# Revit family: Hager-IC-IP40-Plain_Door_1Row-sistema-NoHosted-PT-pt
name_source: partatom
category: Electrical Equipment
units: mm (PartAtom-declared; Revit-internal decimal feet)

## family parameters
Always vertical = Yes
Cut with Voids When Loaded = No
Panel Configuration = Two Columns, Circuits Across
Part Type = Panelboard
Room Calculation Point = No
Round Connector Dimension = Use Diameter
Shared = No
Work Plane-Based = Yes

## types (7) — shared parameters
Classification.Uniclass.Pr.Description = Control circuit device enclosures
Classification.Uniclass.Pr.Number = Pr_80_77_28_16
Default Elevation = 1219 mm
EF000116 - Número RAL = 9010
EF000118 - Com tampa de montagem = No
EF000266 - Número de linhas = 1
EF000339 - Tipo de difusor = EV004216 - Porta
EF001062 - Versão EMC = No
EF005474 - Grau de proteção (IP) = EV006415 - IP40
EF006244 - Tampa/porta transparente = No
EF006306 - Com fecho = No
EF009212 - Tipo de tampa = EV000116 - Fechado
EF015776 - Borne de terra = Yes
EF015777 - Borne de neutro = Yes
EF015941 - Porta para passagem de sinal = Yes
HG000002 - Com porta ou tampa = Yes
HG000003 - Gama = IC
HG000005 - Espessura = 3 mm  [stored 0.00984252 ft]
HG000017 - Distância entre polos = 18 mm  [stored 0.0590551 ft]
Manufacturer = Hager
Type Comments = IC
zero-valued in all types: Cost

## per-type parameters (varying)
| type | EF000003 - Método de montagem | EF000007 - Cor | EF000008 - Largura | EF000040 - Altura | EF000049 - Profundidade | EF000218 - Profundidade incorporada | EF000332 - Altura embutida | EF000846 - Largura para embutir | EF001088 - Extensão possível | EF001131 - Profundidade interior | EF001134 - Calha DIN | EF001596 - Material do corpo | EF002950 - Largura em número de módulos | EF004462 - Tipo de fecho | HG000004 - Referência do Fabricante | HG000006 - Encastrado | Model |
| Montagem em superfície IP40 L170.5 A170 P91 8 unidade de divisão - VD108PP | EV000384 - Montagem em superfície (gesso) | EV000202 - Branco | 170 mm  [stored 0.557743 ft] | 170 mm  [stored 0.557743 ft] | 91 mm  [stored 0.298556 ft] | 0 mm  [stored 0 ft] | 0 mm  [stored 0 ft] | 0 mm  [stored 0 ft] | Yes | 72 mm  [stored 0.23622 ft] | Yes | EV000139 - Plástico | 8 | EV000154 - Outro | VD108PP | No | VD108PP |
| Montagem em superfície IP40 L292.5 A200 P91 12 unidade de divisão - VD112PP | EV000384 - Montagem em superfície (gesso) | EV000202 - Branco | 292 mm  [stored 0.958005 ft] | 200 mm  [stored 0.656168 ft] | 91 mm  [stored 0.298556 ft] | 0 mm  [stored 0 ft] | 0 mm  [stored 0 ft] | 0 mm  [stored 0 ft] | Yes | 72 mm  [stored 0.23622 ft] | Yes | EV000139 - Plástico | 12 | EV000154 - Outro | VD112PP | No | VD112PP |
| Montagem em superfície IP40 L400 A200 P91 18 unidade de divisão - VD118PP | EV000384 - Montagem em superfície (gesso) | EV000202 - Branco | 400 mm  [stored 1.31234 ft] | 200 mm  [stored 0.656168 ft] | 91 mm  [stored 0.298556 ft] | 0 mm  [stored 0 ft] | 0 mm  [stored 0 ft] | 0 mm  [stored 0 ft] | Yes | 72 mm  [stored 0.23622 ft] | Yes | EV000139 - Plástico | 18 | EV000154 - Outro | VD118PP | No | VD118PP |
| Montagem embutida IP40 L236 A206 P91.4 8 unidade de divisão - VR108PP | EV000383 - Montagem embutida (gesso) | EV000202 - Branco | 236 mm | 206 mm  [stored 0.675853 ft] | 91 mm  [stored 0.298556 ft] | 72 mm  [stored 0.23622 ft] | 188 mm  [stored 0.616798 ft] | 218 mm  [stored 0.715223 ft] | Yes | 72 mm  [stored 0.23622 ft] | Yes | EV000139 - Plástico | 8 | EV000154 - Outro | VR108PP | Yes | VR108PP |
| Montagem embutida IP40 L308 A226 P91.4 12 unidade de divisão - VR112PP | EV000383 - Montagem embutida (gesso) | EV000202 - Branco | 308 mm  [stored 1.0105 ft] | 226 mm  [stored 0.74147 ft] | 91 mm  [stored 0.298556 ft] | 72 mm  [stored 0.23622 ft] | 208 mm | 290 mm  [stored 0.951444 ft] | Yes | 72 mm  [stored 0.23622 ft] | Yes | EV000139 - Plástico | 12 | EV000154 - Outro | VR112PP | Yes | VR112PP |
| Montagem embutida IP40 L308 A226 P92 12 unidade de divisão - VR112PPH | EV000383 - Montagem embutida (gesso) |  | 308 mm  [stored 1.0105 ft] | 226 mm  [stored 0.74147 ft] | 92 mm  [stored 0.301837 ft] | 72 mm  [stored 0.23622 ft] | 208 mm | 290 mm  [stored 0.951444 ft] | No | 0 mm  [stored 0 ft] | No |  | 12 |  | VR112PPH | Yes | VR112PPH |
| Montagem embutida IP40 L416 A226 P91.4 18 unidade de divisão - VR118PP | EV000383 - Montagem embutida (gesso) | EV000202 - Branco | 416 mm | 226 mm  [stored 0.74147 ft] | 91 mm  [stored 0.298556 ft] | 72 mm  [stored 0.23622 ft] | 208 mm | 398 mm  [stored 1.30577 ft] | Yes | 72 mm  [stored 0.23622 ft] | Yes | EV000139 - Plástico | 18 | EV000154 - Outro | VR118PP | Yes | VR118PP |

note: [stored X ft] marks values corroborated as IEEE doubles in the binary element streams (Revit-internal decimal feet)

## geometry (parser evidence)
native form markers: Blend x4, Sweep x16
no freeform markers — native parametric forms only
